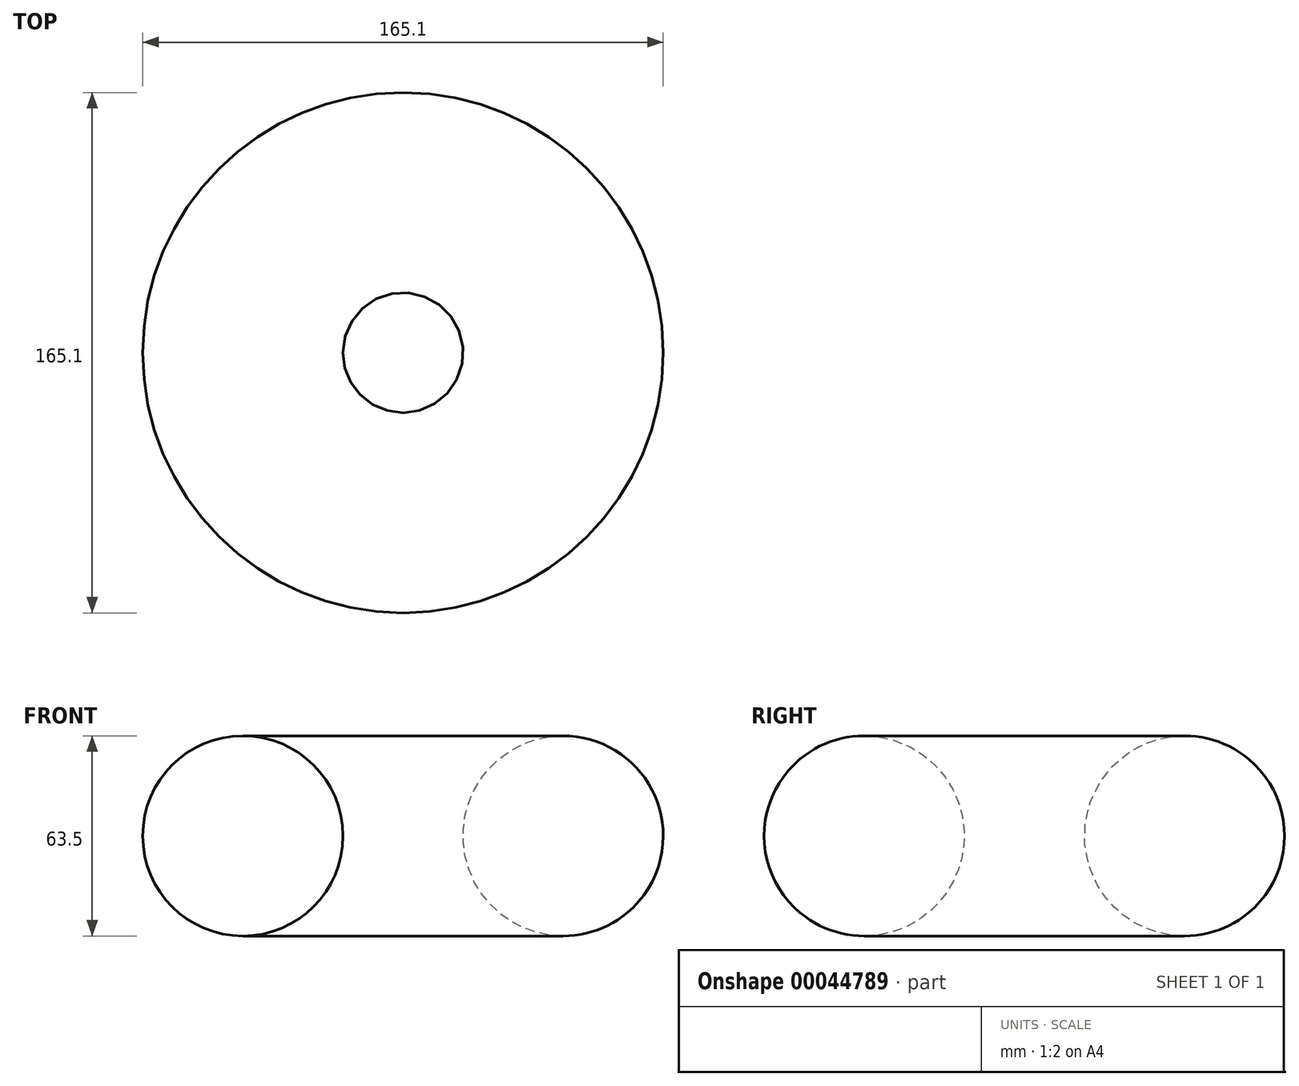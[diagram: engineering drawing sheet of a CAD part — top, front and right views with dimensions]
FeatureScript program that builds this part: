
annotation { "Feature Type Name" : "Feature", "Feature Type Description" : "" }
export const myFeature = defineFeature(function(context is Context, id is Id, definition is map)
    precondition{}
    {
        {
            var Q0;
            Q0=qCreatedBy(makeId("Front.planeOp"),FACE);
            var sketch = newSketch(context, id + "F0", { "sketchPlane" : qUnion([Q0])});
            skLineSegment(sketch, "E0", {"start": v(0, 0) * mm, "end": v(-50.8, 0) * mm});
            skCircle(sketch, "E1", {"center": v(-50.8, 0) * mm, "radius": 31.75 * mm});
            skLineSegment(sketch, "E2", {"start": v(0, 0) * mm, "end": v(0, 64.96) * mm});
            skLineSegment(sketch, "E3", {"start": v(0, 64.96) * mm, "end": v(0, 0) * mm});
            skLineSegment(sketch, "E4", {"start": v(0, -49.91) * mm, "end": v(0, 0) * mm});
            skSolve(sketch);
        }
        {
            var Q0;
            Q0=makeQuery(id+"F0.imprint","IMPRINT",FACE,{"disambiguationData":[TD([[makeQuery(id+"F0.imprint","IMPRINT",EDGE,{"derivedFrom":sQuery(id+"F0.wireOp",EDGE,"E1")}),1.0]])]});
            var Q1;
            Q1=sQuery(id+"F0.wireOp",EDGE,"E4");
            revolve(context, id + "F1", {"entities" : qUnion([Q0]), "axis" : qUnion([Q1]), "revolveType" : RevolveType.FULL});
        }
    });
